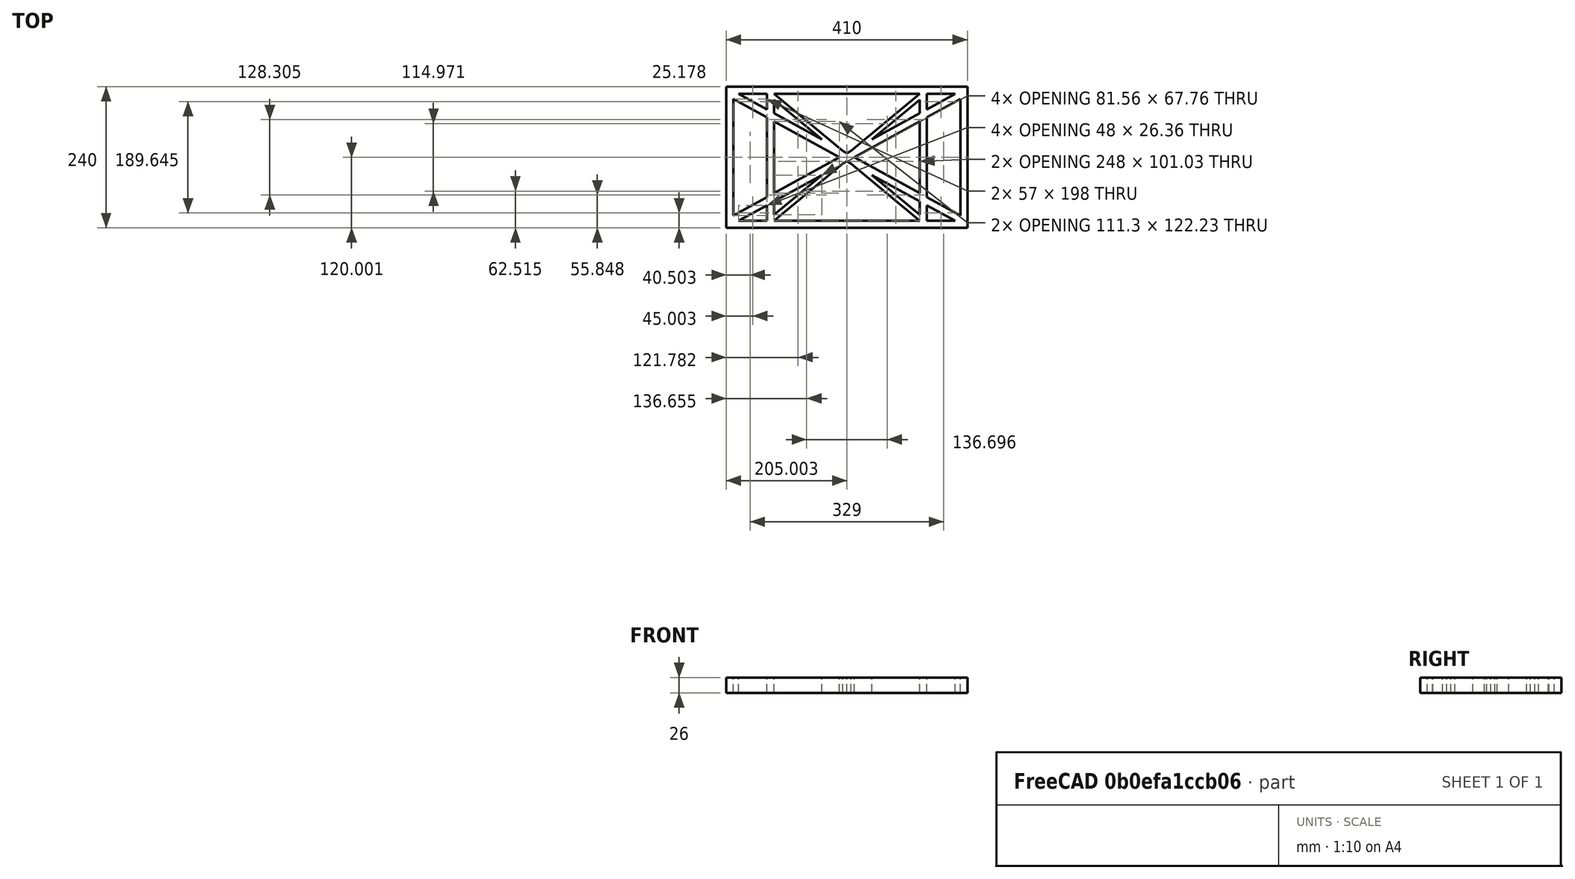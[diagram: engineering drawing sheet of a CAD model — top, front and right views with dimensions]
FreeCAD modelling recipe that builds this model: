
FCSTD DOCUMENT  (FreeCAD 0.19R0.19.2)
Label: laptopStand029
License: All rights reserved
LicenseURL: http://en.wikipedia.org/wiki/All_rights_reserved
objects: Sketcher::SketchObject×3, Part::Extrusion×1
note: 4 computed .brp shape members not serialized (recipe doc carries the construction recipe); baked Part::Feature solids carry a one-line shape summary decoded from their .brp

FEATURE [Sketcher::SketchObject] Sketch
  FullyConstrained = true
  sketch-geometry (52):
    g0: LineSegment StartX=-22.9272 StartY=136.221 StartZ=0 EndX=-22.9272 EndY=-103.779 EndZ=0
    g1: LineSegment StartX=-22.9272 StartY=136.221 StartZ=0 EndX=387.073 EndY=136.221 EndZ=0
    g2: LineSegment StartX=-22.9272 StartY=-103.779 StartZ=0 EndX=387.073 EndY=-103.779 EndZ=0
    g3: LineSegment StartX=387.073 StartY=136.221 StartZ=0 EndX=387.073 EndY=-103.779 EndZ=0
    g4: LineSegment StartX=375.073 StartY=115.221 StartZ=0 EndX=318.073 EndY=83.9235 EndZ=0
    g5: LineSegment StartX=-10.9272 StartY=-82.7794 StartZ=0 EndX=46.0728 EndY=-51.4823 EndZ=0
    g6: LineSegment StartX=-1.92719 StartY=124.221 StartZ=0 EndX=46.0728 EndY=97.8651 EndZ=0
    g7: LineSegment StartX=366.073 StartY=-91.7794 StartZ=0 EndX=318.073 EndY=-65.424 EndZ=0
    g8: LineSegment StartX=-10.9272 StartY=115.221 StartZ=0 EndX=-10.9272 EndY=-82.7794 EndZ=0
    g9: LineSegment StartX=375.073 StartY=-82.7794 StartZ=0 EndX=375.073 EndY=115.221 EndZ=0
    g10: LineSegment StartX=-1.92719 StartY=-91.7794 StartZ=0 EndX=46.0728 EndY=-91.7794 EndZ=0
    g11: LineSegment StartX=318.073 StartY=124.221 StartZ=0 EndX=366.073 EndY=124.221 EndZ=0
    g12: LineSegment StartX=306.073 StartY=-81.8102 StartZ=0 EndX=224.513 EndY=-14.0532 EndZ=0
    g13: LineSegment StartX=58.0728 StartY=114.251 StartZ=0 EndX=139.632 EndY=46.4944 EndZ=0
    g14: LineSegment StartX=306.073 StartY=124.221 StartZ=0 EndX=189.124 EndY=27.0628 EndZ=0
    g15: LineSegment StartX=58.0728 StartY=-91.7794 StartZ=0 EndX=175.022 EndY=5.37834 EndZ=0
    g16: LineSegment StartX=46.0728 StartY=124.221 StartZ=0 EndX=46.0728 EndY=97.8651 EndZ=0
    g17: LineSegment StartX=58.0728 StartY=-81.8102 StartZ=0 EndX=58.0728 EndY=-58.8351 EndZ=0
    g18: LineSegment StartX=318.073 StartY=124.221 StartZ=0 EndX=318.073 EndY=97.8651 EndZ=0
    g19: LineSegment StartX=306.073 StartY=114.251 StartZ=0 EndX=306.073 EndY=91.2763 EndZ=0
    g20: LineSegment StartX=182.073 StartY=23.1914 StartZ=0 EndX=189.124 EndY=27.0628 EndZ=0
    g21: LineSegment StartX=182.073 StartY=9.24976 StartZ=0 EndX=175.022 EndY=5.37834 EndZ=0
    g22: LineSegment StartX=224.513 StartY=46.4944 StartZ=0 EndX=306.073 EndY=114.251 EndZ=0
    g23: LineSegment StartX=175.022 StartY=27.0628 StartZ=0 EndX=58.0728 EndY=124.221 EndZ=0
    g24: LineSegment StartX=169.377 StartY=16.2206 StartZ=0 EndX=58.0728 EndY=77.3346 EndZ=0
    g25: LineSegment StartX=139.632 StartY=-14.0532 StartZ=0 EndX=58.0728 EndY=-81.8102 EndZ=0
    g26: LineSegment StartX=194.768 StartY=16.2206 StartZ=0 EndX=306.073 EndY=-44.8935 EndZ=0
    g27: LineSegment StartX=224.513 StartY=46.4944 StartZ=0 EndX=306.073 EndY=91.2763 EndZ=0
    g28: LineSegment StartX=175.022 StartY=27.0628 StartZ=0 EndX=182.073 EndY=23.1914 EndZ=0
    g29: LineSegment StartX=139.632 StartY=-14.0532 StartZ=0 EndX=58.0728 EndY=-58.8351 EndZ=0
    g30: LineSegment StartX=189.124 StartY=5.37834 StartZ=0 EndX=182.073 EndY=9.24976 EndZ=0
    g31: LineSegment StartX=189.124 StartY=5.37834 StartZ=0 EndX=306.073 EndY=-91.7794 EndZ=0
    g32: LineSegment StartX=306.073 StartY=77.3346 StartZ=0 EndX=306.073 EndY=-44.8935 EndZ=0
    g33: LineSegment StartX=318.073 StartY=83.9235 StartZ=0 EndX=318.073 EndY=-51.4823 EndZ=0
    g34: LineSegment StartX=318.073 StartY=97.8651 StartZ=0 EndX=366.073 EndY=124.221 EndZ=0
    g35: LineSegment StartX=306.073 StartY=77.3346 StartZ=0 EndX=194.768 EndY=16.2206 EndZ=0
    g36: LineSegment StartX=306.073 StartY=-58.8351 StartZ=0 EndX=224.513 EndY=-14.0532 EndZ=0
    g37: LineSegment StartX=306.073 StartY=-58.8351 StartZ=0 EndX=306.073 EndY=-81.8102 EndZ=0
    g38: LineSegment StartX=318.073 StartY=-51.4823 StartZ=0 EndX=375.073 EndY=-82.7794 EndZ=0
    g39: LineSegment StartX=318.073 StartY=-65.424 StartZ=0 EndX=318.073 EndY=-91.7794 EndZ=0
    g40: LineSegment StartX=306.073 StartY=124.221 StartZ=0 EndX=58.0728 EndY=124.221 EndZ=0
    g41: LineSegment StartX=318.073 StartY=-91.7794 StartZ=0 EndX=366.073 EndY=-91.7794 EndZ=0
    g42: LineSegment StartX=58.0728 StartY=-91.7794 StartZ=0 EndX=306.073 EndY=-91.7794 EndZ=0
    g43: LineSegment StartX=58.0728 StartY=-44.8935 StartZ=0 EndX=58.0728 EndY=77.3346 EndZ=0
    g44: LineSegment StartX=46.0728 StartY=-65.424 StartZ=0 EndX=-1.92719 EndY=-91.7794 EndZ=0
    g45: LineSegment StartX=46.0728 StartY=-65.424 StartZ=0 EndX=46.0728 EndY=-91.7794 EndZ=0
    g46: LineSegment StartX=58.0728 StartY=-44.8935 StartZ=0 EndX=169.377 EndY=16.2206 EndZ=0
    g47: LineSegment StartX=58.0728 StartY=91.2763 StartZ=0 EndX=58.0728 EndY=114.251 EndZ=0
    g48: LineSegment StartX=46.0728 StartY=83.9235 StartZ=0 EndX=46.0728 EndY=-51.4823 EndZ=0
    g49: LineSegment StartX=46.0728 StartY=124.221 StartZ=0 EndX=-1.92719 EndY=124.221 EndZ=0
    g50: LineSegment StartX=58.0728 StartY=91.2763 StartZ=0 EndX=139.632 EndY=46.4944 EndZ=0
    g51: LineSegment StartX=46.0728 StartY=83.9235 StartZ=0 EndX=-10.9272 EndY=115.221 EndZ=0
  constraints (102):
    c: Vertical(g0)
    c: Distance(g0) = 240
    c: Horizontal(g1)
    c: Distance(g1) = 410
    c: Coincident(g1,g0)
    c: Coincident(g2,g0)
    c: Horizontal(g2)
    c: Coincident(g3,g1)
    c: Vertical(g3)
    c: Coincident(g2,g3)
    c: Block(g1)
    c: Horizontal(g10)
    c: Horizontal(g11)
    c: PointOnObject(g35,g6)
    c: Coincident(g28,g20)
    c: Coincident(g30,g21)
    c: Tangent(g7,g24)
    c: PointOnObject(g24,g5)
    c: PointOnObject(g26,g4)
    c: Coincident(g20,g14)
    c: Tangent(g20,g27)
    c: Coincident(g50,g13)
    c: Coincident(g28,g23)
    c: Coincident(g22,g27)
    c: Coincident(g21,g15)
    c: Coincident(g29,g25)
    c: Tangent(g21,g29)
    c: Coincident(g36,g12)
    c: Coincident(g31,g30)
    c: Coincident(g22,g19)
    c: Tangent(g19,g32)
    c: Tangent(g18,g33)
    c: Coincident(g27,g19)
    c: Tangent(g27,g34)
    c: Coincident(g4,g33)
    c: Coincident(g35,g32)
    c: Tangent(g4,g35)
    c: Coincident(g37,g12)
    c: Tangent(g7,g36)
    c: Tangent(g32,g37)
    c: Coincident(g26,g32)
    c: Tangent(g26,g38)
    c: Coincident(g33,g38)
    c: Coincident(g39,g7)
    c: Tangent(g33,g39)
    c: Coincident(g25,g17)
    c: Tangent(g17,g43)
    c: Coincident(g29,g17)
    c: Tangent(g29,g44)
    c: Coincident(g45,g44)
    c: Tangent(g16,g45)
    c: Coincident(g5,g48)
    c: Coincident(g46,g43)
    c: Tangent(g5,g46)
    c: Tangent(g43,g47)
    c: Tangent(g16,g48)
    c: Coincident(g13,g47)
    c: PointOnObject(g40,g23)
    c: Tangent(g40,g49)
    c: Coincident(g6,g16)
    c: Coincident(g50,g47)
    c: Tangent(g6,g50)
    c: Coincident(g24,g43)
    c: Coincident(g51,g48)
    c: Tangent(g24,g51)
    c: Block(g23)
    c: Block(g14)
    c: Block(g20)
    c: Block(g40)
    c: Block(g18)
    c: Block(g34)
    c: Block(g4)
    c: Block(g38)
    c: Block(g9)
    c: Block(g36)
    c: Block(g37)
    c: Block(g7)
    c: Block(g39)
    c: Block(g22)
    c: Block(g31)
    c: Block(g42)
    c: Block(g21)
    c: Block(g15)
    c: Block(g29)
    c: Block(g25)
    c: Block(g45)
    c: Block(g44)
    c: Block(g5)
    c: Block(g8)
    c: Block(g51)
    c: Block(g6)
    c: Block(g16)
    c: Block(g13)
    c: Block(g47)
    c: Block(g35)
    c: Block(g32)
    c: Block(g24)
    c: Block(g46)
    c: Block(g49)
    c: Block(g11)
    c: Block(g41)
    c: Block(g10)
FEATURE [Part::Extrusion] Extrude
  Base = -> Sketch
  Dir = (0,0,1)
  DirMode = 2
  FaceMakerClass = Part::FaceMakerBullseye
  LengthFwd = 26
  LengthRev = 0
  Solid = true
  Symmetric = false
FEATURE [Sketcher::SketchObject] Sketch001
  FullyConstrained = true
  MapMode = 4
  Placement = pos=(0,0,0) rot=(0.57735,0.57735,0.57735;2.0944rad)
  Support = -> [Sketch]
  sketch-geometry (33):
    g0: LineSegment StartX=17.2232 StartY=-16.0875 StartZ=0 EndX=117.223 EndY=-16.0875 EndZ=0
    g1: LineSegment StartX=17.2232 StartY=-16.0875 StartZ=0 EndX=17.2232 EndY=-19.0875 EndZ=0
    g2: LineSegment StartX=117.223 StartY=-16.0875 StartZ=0 EndX=117.223 EndY=-19.0875 EndZ=0
    g3: BSplineCurve PolesCount=3 KnotsCount=2 Degree=2 IsPeriodic=0
    g4: LineSegment StartX=-9.4377 StartY=-200.664 StartZ=0 EndX=24.2583 EndY=-213.335 EndZ=0
    g5: LineSegment StartX=17.2232 StartY=-19.0875 StartZ=0 EndX=29.8094 EndY=-19.0875 EndZ=0
    g6: ArcOfCircle CenterX=73.122 CenterY=-32.2909 CenterZ=0 NormalX=0 NormalY=0 NormalZ=1 AngleXU=0 Radius=13 StartAngle=5.92268 EndAngle=9.06428
    g7: LineSegment StartX=85.2864 StartY=-36.8765 StartZ=0 EndX=78.9505 EndY=-53.7246 EndZ=0
    g8: LineSegment StartX=60.9577 StartY=-27.7052 StartZ=0 EndX=54.6191 EndY=-44.5532 EndZ=0
    g9: ArcOfCircle CenterX=66.7816 CenterY=-49.1439 CenterZ=0 NormalX=0 NormalY=0 NormalZ=1 AngleXU=0 Radius=13 StartAngle=2.78068 EndAngle=5.92131
    g10: ArcOfCircle CenterX=55.9263 CenterY=-78.1807 CenterZ=0 NormalX=0 NormalY=0 NormalZ=1 AngleXU=0 Radius=13 StartAngle=5.92268 EndAngle=9.06428
    g11: LineSegment StartX=68.0907 StartY=-82.7664 StartZ=0 EndX=61.7547 EndY=-99.6148 EndZ=0
    g12: ArcOfCircle CenterX=49.5884 CenterY=-95.0342 CenterZ=0 NormalX=0 NormalY=0 NormalZ=1 AngleXU=0 Radius=13 StartAngle=2.78068 EndAngle=5.92131
    g13: LineSegment StartX=43.7619 StartY=-73.595 StartZ=0 EndX=37.426 EndY=-90.4435 EndZ=0
    g14: ArcOfCircle CenterX=38.7206 CenterY=-124.067 CenterZ=0 NormalX=0 NormalY=0 NormalZ=1 AngleXU=0 Radius=13 StartAngle=5.92268 EndAngle=9.06428
    g15: LineSegment StartX=26.5562 StartY=-119.481 StartZ=0 EndX=20.2251 EndY=-136.329 EndZ=0
    g16: ArcOfCircle CenterX=32.3875 CenterY=-140.92 CenterZ=0 NormalX=0 NormalY=0 NormalZ=1 AngleXU=0 Radius=13 StartAngle=2.78068 EndAngle=5.92131
    g17: LineSegment StartX=50.885 StartY=-128.652 StartZ=0 EndX=44.549 EndY=-145.5 EndZ=0
    g18: ArcOfCircle CenterX=21.4715 CenterY=-169.934 CenterZ=0 NormalX=0 NormalY=0 NormalZ=1 AngleXU=0 Radius=13 StartAngle=5.92268 EndAngle=9.06428
    g19: LineSegment StartX=9.3071 StartY=-165.349 StartZ=0 EndX=2.97115 EndY=-182.197 EndZ=0
    g20: ArcOfCircle CenterX=15.1336 CenterY=-186.787 CenterZ=0 NormalX=0 NormalY=0 NormalZ=1 AngleXU=0 Radius=13 StartAngle=2.78068 EndAngle=5.92131
    g21: LineSegment StartX=33.6358 StartY=-174.52 StartZ=0 EndX=27.2999 EndY=-191.368 EndZ=0
    g22: LineSegment StartX=24.2583 StartY=-213.335 StartZ=0 EndX=25.4551 EndY=-210.153 EndZ=0
    g23: LineSegment StartX=-9.4377 StartY=-200.664 StartZ=0 EndX=-8.24091 EndY=-197.481 EndZ=0
    g24: LineSegment StartX=94.6577 StartY=-26.1351 StartZ=0 EndX=25.4551 EndY=-210.153 EndZ=0
    g25-g28: Circle x4 (B-spline internal-alignment scaffolding for g29; pole/knot coordinates omitted)
    g29: BSplineCurve PolesCount=4 KnotsCount=2 Degree=3 IsPeriodic=0
    g30: GeomPoint X=28.8094 Y=-19.0875 Z=0
    g31: GeomPoint X=47.0443 Y=-50.4712 Z=0
    g32: LineSegment StartX=47.3963 StartY=-49.5352 StartZ=0 EndX=-8.24091 EndY=-197.481 EndZ=0
  constraints (62):
    c: Horizontal(g0)
    c: Distance(g0) = 100
    c: Block(g0)
    c: Coincident(g1,g0)
    c: Vertical(g1)
    c: Distance(g1) = 3
    c: Coincident(g2,g0)
    c: Vertical(g2)
    c: Distance(g2) = 3
    c: Block(g3)
    c: Coincident(g3,g2)
    c: Coincident(g5,g1)
    c: Horizontal(g5)
    c: Block(g6)
    c: Distance(g7) = 18
    c: Coincident(g7,g6)
    c: Coincident(g8,g6)
    c: Block(g9)
    c: Coincident(g9,g8)
    c: Block(g8)
    c: Coincident(g11,g10)
    c: Coincident(g13,g10)
    c: Block(g12)
    c: Coincident(g12,g13)
    c: Block(g13)
    c: Block(g10)
    c: Block(g11)
    c: Coincident(g17,g14)
    c: Coincident(g15,g14)
    c: Block(g16)
    c: Coincident(g16,g15)
    c: Block(g15)
    c: Block(g14)
    c: Coincident(g21,g18)
    c: Coincident(g19,g18)
    c: Block(g20)
    c: Coincident(g20,g19)
    c: Block(g19)
    c: Block(g18)
    c: Distance(g21) = 18
    c: Block(g21)
    c: Block(g17)
    c: Distance(g22) = 3.4
    c: Coincident(g23,g4)
    c: Coincident(g24,g3)
    c: Coincident(g24,g22)
    c: Coincident(g32,g23)
    c: Block(g24)
    c: Block(g4)
    c: Block(g22)
    c: Block(g7)
    c: Weight(g25) = 1
    c: Equal(g25,g26)
    c: Equal(g25,g27)
    c: Equal(g25,g28)
    c: InternalAlignment(g25-g28 -> g29) x4
    c: InternalAlignment(g30,g29)
    c: InternalAlignment(g31,g29)
    c: PointOnObject(g32,g28)
    c: PointOnObject(g5,g25)
    c: Block(g29)
    c: Block(g32)
FEATURE [Sketcher::SketchObject] Sketch002
  FullyConstrained = true
  Placement = pos=(0,0,0) rot=(-1,0,0;4.71239rad)
